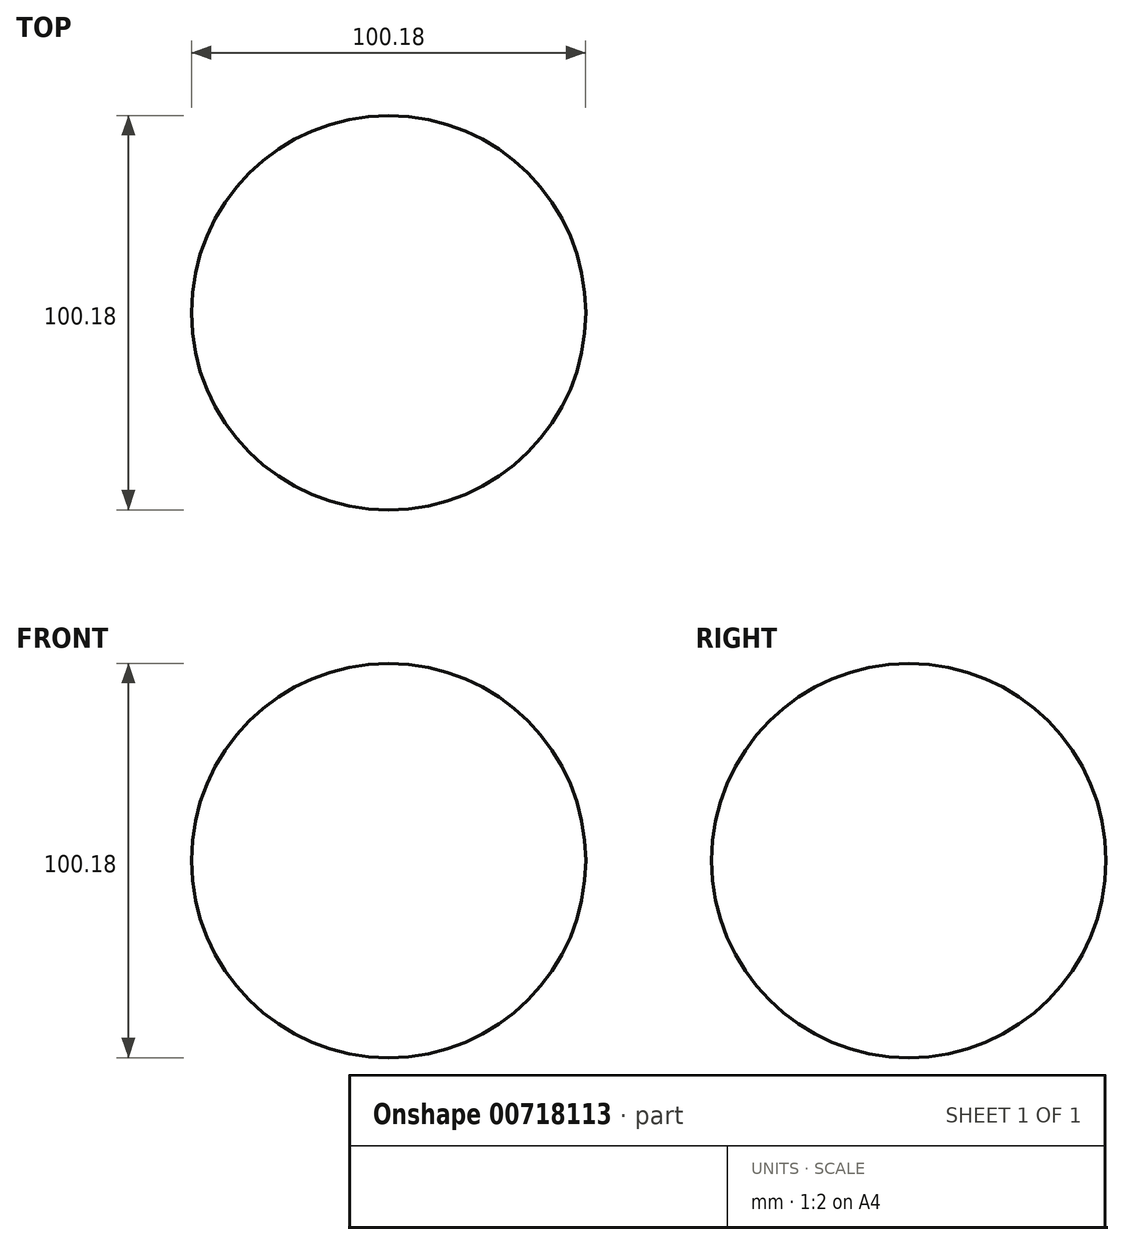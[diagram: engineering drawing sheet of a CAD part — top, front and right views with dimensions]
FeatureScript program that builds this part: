
annotation { "Feature Type Name" : "Feature", "Feature Type Description" : "" }
export const myFeature = defineFeature(function(context is Context, id is Id, definition is map)
    precondition{}
    {
        {
            var Q0;
            Q0=qCreatedBy(makeId("Top.planeOp"),FACE);
            var sketch = newSketch(context, id + "F0", { "sketchPlane" : qUnion([Q0])});
            skCircle(sketch, "E0", {"center": v(0, 0) * mm, "radius": 50.1 * mm});
            skLineSegment(sketch, "E1", {"start": v(0, 50.1) * mm, "end": v(0, -50.1) * mm});
            skSolve(sketch);
        }
        {
            var Q0;
            {var subQ0=sQuery(id+"F0.wireOp",EDGE,"E1");Q0=makeQuery(id+"F0.imprint","IMPRINT",FACE,{"disambiguationData":[TD([[makeQuery(id+"F0.imprint","IMPRINT",EDGE,{"derivedFrom":subQ0}),1.0]])]});}
            var Q1;
            Q1=sQuery(id+"F0.wireOp",EDGE,"E1");
            revolve(context, id + "F1", {"surfaceOperationType" : NewSurfaceOperationType.NEW, "entities" : qUnion([Q0]), "axis" : qUnion([Q1]), "revolveType" : RevolveType.FULL});
        }
    });
